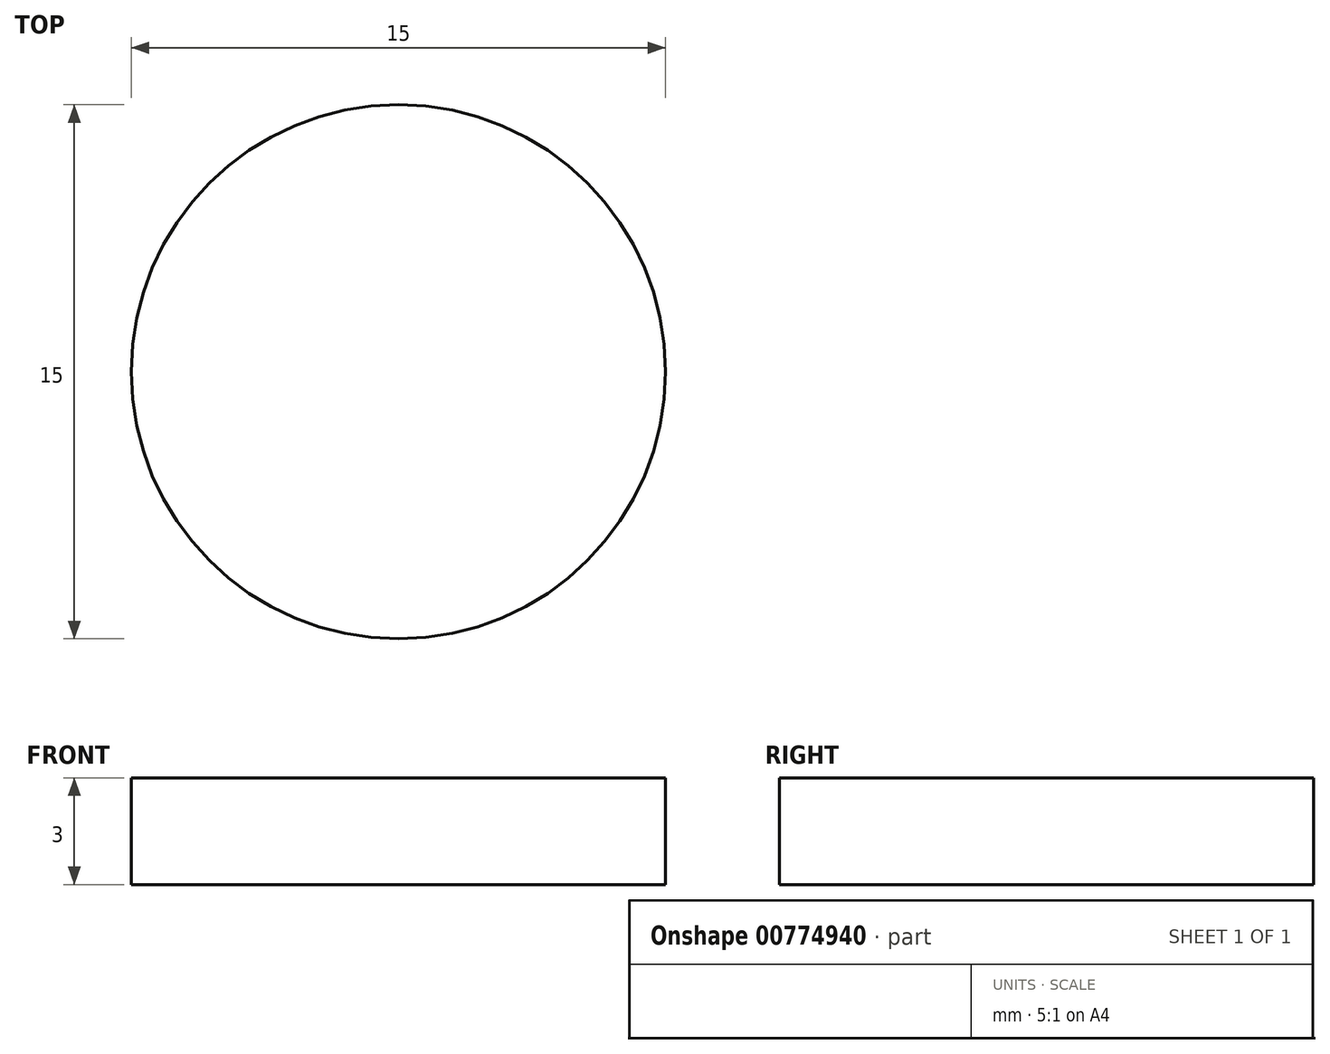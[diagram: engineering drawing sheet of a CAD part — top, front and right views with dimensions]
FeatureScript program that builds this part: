
annotation { "Feature Type Name" : "Feature", "Feature Type Description" : "" }
export const myFeature = defineFeature(function(context is Context, id is Id, definition is map)
    precondition{}
    {
        {
            var Q0;
            Q0=qCreatedBy(makeId("Top.planeOp"),FACE);
            var sketch = newSketch(context, id + "F0", { "sketchPlane" : qUnion([Q0])});
            skCircle(sketch, "E0", {"center": v(0, 0) * mm, "radius": 7.5 * mm});
            skSolve(sketch);
        }
        {
            var Q0;
            Q0 = qSketchRegion(id + "F0", true);
            extrude(context, id + "F1", {"entities" : qUnion([Q0]), "depth" : 3 * mm, "offsetDistance" : 25 * mm});
        }
    });
